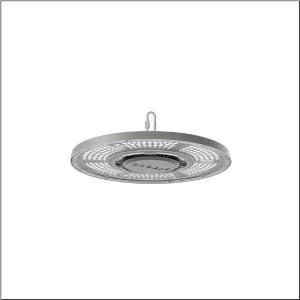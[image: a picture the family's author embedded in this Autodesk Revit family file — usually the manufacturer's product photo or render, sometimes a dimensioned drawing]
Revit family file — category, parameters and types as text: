
# Revit family: highbay_31-s_51hc427a4fmb
name_source: partatom
category: Lighting Fixtures
units: mm (PartAtom-declared; Revit-internal decimal feet)

## family parameters
Cut with Voids When Loaded = No
Host = Face
Light Source = No
Part Type = Normal
Room Calculation Point = No
Round Connector Dimension = Use Diameter
Shared = No

## types (1)
- Highbay 31-S (1 x LED, 14000 lm, 94 W, 4000K)
    Apparent Load = 94 VA
    CIE Flux Codes = 77 99 100 100 100
    Color Rendering = 80
    Color Temperature = 4000K
    Default Elevation = 1800 mm
    Description = Highbay 31-S, LED high bay luminaire, primary light control with lens, of PC, primary optical cover: cover panel, of PC, transparent, light emission: direct distribution, primary light characteristic: rotationally symmetric, installation type: suspended mounting, surface-mounted, LED, rated luminous flux: 14.000lm, luminous efficacy: 150lm/W, light colour: 840, colour temperature: 4000K, control gear: ECG, with cable, 3x 1.0mm², free wire ends, mains connection: 220..240V, AC/DC, 0/50..60Hz, cable length: 1,5m, rated input power: 94W, housing, rotationally symmetric, of diecast aluminium, powder-coated, grey aluminium (RAL 9007), with hook on luminaire side, incl. screw, diameter: 339mm, protection rating (complete): IP65, insulation class (complete): insulation class I (protective earthing), certification: CE, ENEC, UKCA, protection symbol: D, impact resistance: IK08, permissible operating ambient temperature: -30..+45°C, standard: EN 60598-2-22, EN 60598, corresponds to IFS (International Featured Standards) requirements for safety and quality in the food industry, packaging unit: 1 piece
    Height = 141 mm
    Lamp = 1 x LED
    Lamp Light Flux = 14000 lm
    Lamp Power = 94 W
    Lamp count = 1
    Length = 339 mm
    Luminous efficacy = 149 lm/W
    Manufacturer = Siteco
    ModVariant = No
    Model = 51HC427A4FMB
    Mounting Place = Ceiling
    Mounting Type = Pendant
    Number of Poles = 1
    OnlyDefault = Yes
    Power Factor = 1
    Product Name = Highbay 31-S
    Product group = LED high bay luminaire
    ProductGroupID = 903
    Protection Class = Protection class I
    Protection Degree = IP 65
    RLX_Detail_Level = 1
    RLX_Emergency_Light_Flux = 0 lm
    RLX_Emergency_Type = 0
    RLX_Emergency_Type_DB = No
    RlxData = <blob elided: 163689 chars, md5=3a63417b>
    Socket = socket
    Standby Power = 0 W
    System Light Flux = 14000 lm
    System Power = 94 W
    Type Comments = Product without accessories
    Type Image = l_1007237.jpg
    URL = http://relux.com
    VarID = ---
    Voltage = 0 V
    Weight = 0.00 kg
    Width = 0 mm  [stored 0 ft]

note: [stored X ft] marks values corroborated as IEEE doubles in the binary element streams (Revit-internal decimal feet)

## geometry (parser evidence)
native form markers: Blend x4, Sweep x10
no freeform markers — native parametric forms only
